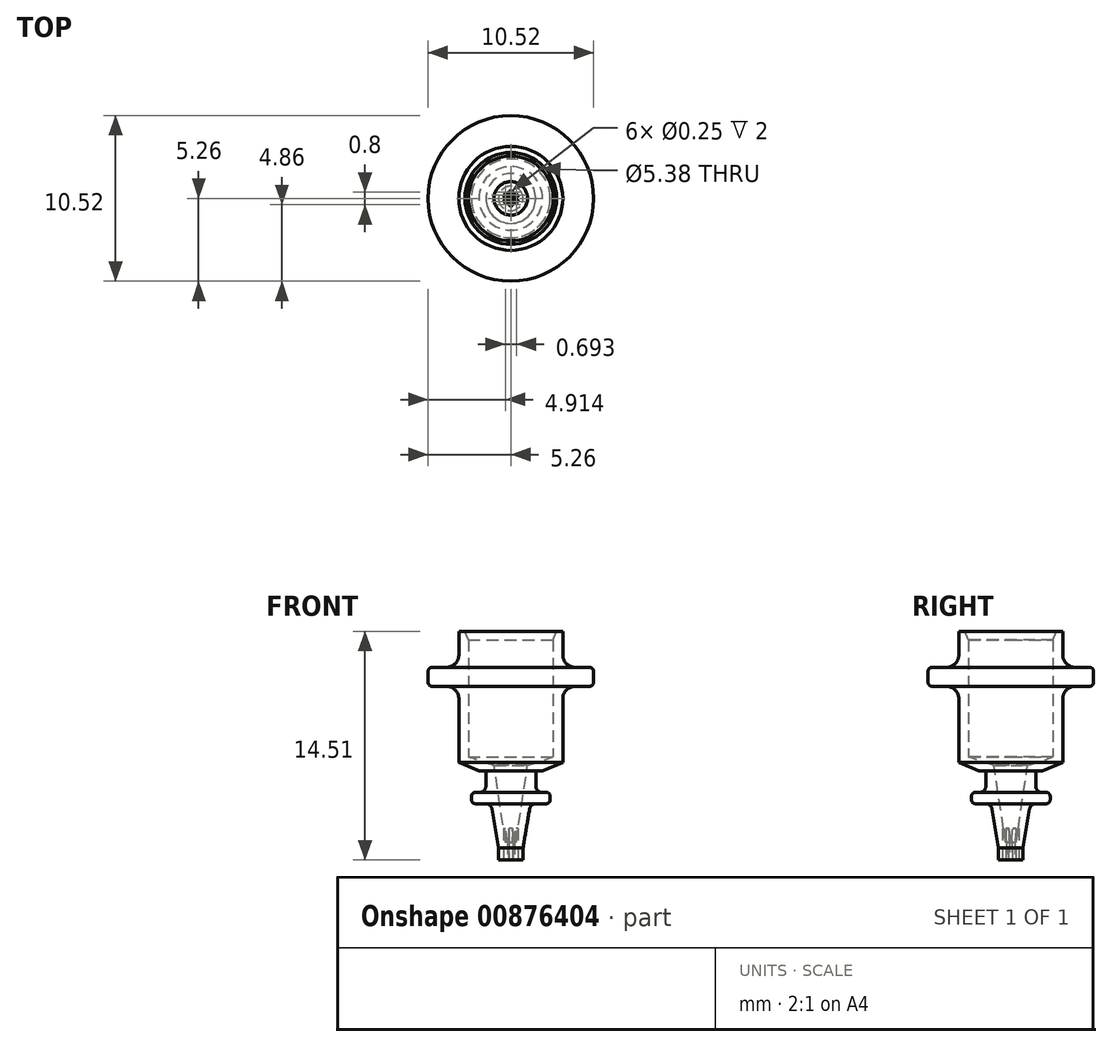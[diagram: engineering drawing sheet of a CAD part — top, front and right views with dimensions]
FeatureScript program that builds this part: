
annotation { "Feature Type Name" : "Feature", "Feature Type Description" : "" }
export const myFeature = defineFeature(function(context is Context, id is Id, definition is map)
    precondition{}
    {
        {
            var Q0;
            Q0=qCreatedBy(makeId("Front.planeOp"),FACE);
            var sketch = newSketch(context, id + "F0", { "sketchPlane" : qUnion([Q0])});
            skLineSegment(sketch, "E0", {"start": v(0.77, 0.76) * mm, "end": v(1.25, 3.57) * mm});
            skLineSegment(sketch, "E1", {"start": v(1.25, 3.57) * mm, "end": v(2.5, 3.57) * mm});
            skLineSegment(sketch, "E2", {"start": v(2.5, 3.57) * mm, "end": v(2.5, 4.3) * mm});
            skLineSegment(sketch, "E3", {"start": v(2.5, 4.3) * mm, "end": v(1.58, 4.3) * mm});
            skLineSegment(sketch, "E4", {"start": v(1.58, 4.3) * mm, "end": v(1.58, 5.66) * mm});
            skLineSegment(sketch, "E5", {"start": v(1.58, 5.66) * mm, "end": v(2.02, 5.66) * mm});
            skLineSegment(sketch, "E6", {"start": v(3.3, 6.2) * mm, "end": v(2.02, 5.66) * mm});
            skLineSegment(sketch, "E7", {"start": v(3.3, 6.2) * mm, "end": v(3.3, 11.03) * mm});
            skLineSegment(sketch, "E8", {"start": v(3.3, 11.03) * mm, "end": v(5.25, 11.03) * mm});
            skLineSegment(sketch, "E9", {"start": v(5.25, 11.03) * mm, "end": v(5.25, 12.23) * mm});
            skLineSegment(sketch, "E10", {"start": v(5.25, 12.23) * mm, "end": v(3.3, 12.23) * mm});
            skLineSegment(sketch, "E11", {"start": v(3.3, 12.23) * mm, "end": v(3.3, 14.5) * mm});
            skLineSegment(sketch, "E12", {"start": v(3.3, 14.5) * mm, "end": v(2.91, 14.5) * mm});
            skLineSegment(sketch, "E13", {"start": v(2.91, 14.51) * mm, "end": v(2.7, 13.98) * mm});
            skLineSegment(sketch, "E14", {"start": v(2.69, 13.98) * mm, "end": v(2.7, 6.54) * mm});
            skLineSegment(sketch, "E15", {"start": v(2.7, 6.54) * mm, "end": v(1.06, 5.99) * mm});
            skLineSegment(sketch, "E16", {"start": v(1.06, 5.99) * mm, "end": v(0.34, 1.1) * mm});
            skLineSegment(sketch, "E17", {"start": v(0.34, 1.1) * mm, "end": v(0.13, 1.1) * mm});
            skLineSegment(sketch, "E18", {"start": v(0.13, 1.1) * mm, "end": v(0.13, 0) * mm});
            skLineSegment(sketch, "E19", {"start": v(0, 0) * mm, "end": v(0, 1.24) * mm, "construction": true});
            skLineSegment(sketch, "E20", {"start": v(0.78, 0.76) * mm, "end": v(0.78, 0) * mm});
            skLineSegment(sketch, "E21", {"start": v(0.78, 0) * mm, "end": v(0.12, 0) * mm});
            skSolve(sketch);
        }
        {
            var Q0;
            Q0=makeQuery(id+"F0.imprint","IMPRINT",FACE,{"disambiguationData":[TD([[makeQuery(id+"F0.imprint","IMPRINT",EDGE,{"derivedFrom":sQuery(id+"F0.wireOp",EDGE,"e6LHfJcI-CbRT-moQV-SlZ1-dI7YaycNfLPc")}),1.0]])]});
            var Q1;
            Q1=makeQuery(id+"F0.imprint","IMPRINT",FACE,{"disambiguationData":[TD([[makeQuery(id+"F0.imprint","IMPRINT",EDGE,{"derivedFrom":sQuery(id+"F0.wireOp",EDGE,"E0")}),1.0]])]});
            var Q2;
            Q2=sQuery(id+"F0.wireOp",EDGE,"E19");
            revolve(context, id + "F1", {"surfaceOperationType" : NewSurfaceOperationType.NEW, "entities" : qUnion([Q0, Q1]), "axis" : qUnion([Q2]), "revolveType" : RevolveType.FULL});
        }
        {
            var Q0;
            Q0=makeQuery(id+"F1.opRevolve","SWEPT_EDGE",EDGE,{"disambiguationData":[OSD([sQuery(id+"F0.wireOp",EDGE,"E9"),sQuery(id+"F0.wireOp",EDGE,"E10")])]});
            var Q1;
            Q1=makeQuery(id+"F1.opRevolve","SWEPT_EDGE",EDGE,{"disambiguationData":[OSD([sQuery(id+"F0.wireOp",EDGE,"E8"),sQuery(id+"F0.wireOp",EDGE,"E9")])]});
            var Q2;
            Q2=makeQuery(id+"F1.opRevolve","SWEPT_EDGE",EDGE,{"disambiguationData":[OSD([sQuery(id+"F0.wireOp",EDGE,"E2"),sQuery(id+"F0.wireOp",EDGE,"E3")])]});
            var Q3;
            Q3=makeQuery(id+"F1.opRevolve","SWEPT_EDGE",EDGE,{"disambiguationData":[OSD([sQuery(id+"F0.wireOp",EDGE,"E1"),sQuery(id+"F0.wireOp",EDGE,"E2")])]});
            fillet(context, id + "F2", {"entities" : qUnion([Q0, Q1, Q2, Q3]), "radius" : 0.25 * mm, "tangentPropagation" : true, "allowEdgeOverflow" : false});
        }
        {
            var Q0;
            Q0=makeQuery(id+"F1.opRevolve","SWEPT_EDGE",EDGE,{"disambiguationData":[OSD([sQuery(id+"F0.wireOp",EDGE,"E10"),sQuery(id+"F0.wireOp",EDGE,"E11")])]});
            var Q1;
            Q1=makeQuery(id+"F1.opRevolve","SWEPT_EDGE",EDGE,{"disambiguationData":[OSD([sQuery(id+"F0.wireOp",EDGE,"E7"),sQuery(id+"F0.wireOp",EDGE,"E8")])]});
            fillet(context, id + "F3", {"entities" : qUnion([Q0, Q1]), "radius" : 0.8 * mm, "tangentPropagation" : true, "allowEdgeOverflow" : false});
        }
        {
            var Q0;
            Q0=makeQuery(id+"F1.opRevolve","SWEPT_EDGE",EDGE,{"disambiguationData":[OSD([sQuery(id+"F0.wireOp",EDGE,"E3"),sQuery(id+"F0.wireOp",EDGE,"E4")])]});
            var Q1;
            Q1=makeQuery(id+"F1.opRevolve","SWEPT_EDGE",EDGE,{"disambiguationData":[OSD([sQuery(id+"F0.wireOp",EDGE,"E0"),sQuery(id+"F0.wireOp",EDGE,"E1")])]});
            fillet(context, id + "F4", {"entities" : qUnion([Q0, Q1]), "radius" : 0.4 * mm, "tangentPropagation" : true, "allowEdgeOverflow" : false});
        }
        {
            var Q0;
            Q0=makeQuery(id+"F1.opRevolve","SWEPT_FACE",FACE,{"disambiguationData":[OSD([sQuery(id+"F0.wireOp",EDGE,"E21")])]});
            var sketch = newSketch(context, id + "F5", { "sketchPlane" : qUnion([Q0])});
            skCircle(sketch, "E22", {"center": v(0, 0.4) * mm, "radius": 0.12 * mm});
            skCircle(sketch, "E23.1.0", {"center": v(-0.35, 0.2) * mm, "radius": 0.12 * mm});
            skCircle(sketch, "E23.2.0", {"center": v(-0.35, -0.2) * mm, "radius": 0.12 * mm});
            skCircle(sketch, "E23.3.0", {"center": v(0, -0.4) * mm, "radius": 0.12 * mm});
            skCircle(sketch, "E23.4.0", {"center": v(0.35, -0.2) * mm, "radius": 0.12 * mm});
            skCircle(sketch, "E23.5.0", {"center": v(0.35, 0.2) * mm, "radius": 0.12 * mm});
            skPoint(sketch, "E23.center", {"position": v(0, 0) * mm});
            skSolve(sketch);
        }
        {
            var Q0;
            Q0=makeQuery(id+"F5.imprint","IMPRINT",FACE,{"disambiguationData":[TD([[makeQuery(id+"F5.imprint","IMPRINT",EDGE,{"derivedFrom":sQuery(id+"F5.wireOp",EDGE,"E22")}),1.0]])]});
            var Q1;
            Q1=makeQuery(id+"F5.imprint","IMPRINT",FACE,{"disambiguationData":[TD([[makeQuery(id+"F5.imprint","IMPRINT",EDGE,{"derivedFrom":sQuery(id+"F5.wireOp",EDGE,"E23.1.0")}),1.0]])]});
            var Q2;
            Q2=makeQuery(id+"F5.imprint","IMPRINT",FACE,{"disambiguationData":[TD([[makeQuery(id+"F5.imprint","IMPRINT",EDGE,{"derivedFrom":sQuery(id+"F5.wireOp",EDGE,"E23.2.0")}),1.0]])]});
            var Q3;
            Q3=makeQuery(id+"F5.imprint","IMPRINT",FACE,{"disambiguationData":[TD([[makeQuery(id+"F5.imprint","IMPRINT",EDGE,{"derivedFrom":sQuery(id+"F5.wireOp",EDGE,"E23.3.0")}),1.0]])]});
            var Q4;
            Q4=makeQuery(id+"F5.imprint","IMPRINT",FACE,{"disambiguationData":[TD([[makeQuery(id+"F5.imprint","IMPRINT",EDGE,{"derivedFrom":sQuery(id+"F5.wireOp",EDGE,"E23.4.0")}),1.0]])]});
            var Q5;
            Q5=makeQuery(id+"F5.imprint","IMPRINT",FACE,{"disambiguationData":[TD([[makeQuery(id+"F5.imprint","IMPRINT",EDGE,{"derivedFrom":sQuery(id+"F5.wireOp",EDGE,"E23.5.0")}),1.0]])]});
            extrude(context, id + "F6", {"entities" : qUnion([Q0, Q1, Q2, Q3, Q4, Q5]), "operationType" : NewBodyOperationType.REMOVE, "oppositeDirection" : true, "depth" : 2 * mm, "offsetDistance" : 25 * mm});
        }
    });
